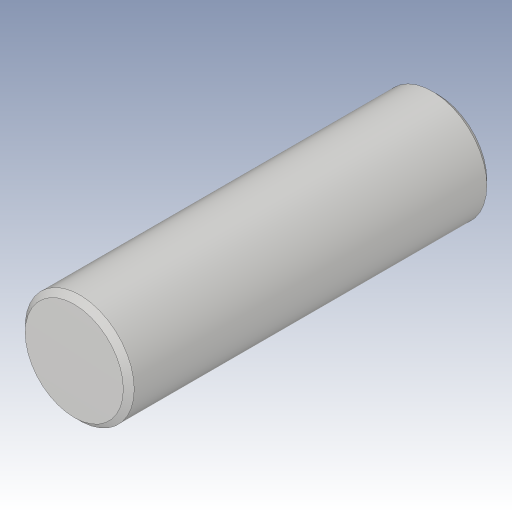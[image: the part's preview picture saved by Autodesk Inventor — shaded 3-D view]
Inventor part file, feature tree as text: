
AUTODESK INVENTOR PART (.ipt)
format: ipt  version: 2023.3 (Build 273359000, 359)  size: 141,312 bytes
history: native  units: in
note: dims shown in document units (in); Inventor stores cm internally (conversion verified against a paired STEP export)
features: extrude x1, chamfer x1, sketch x1
ambient origin geometry x8: Origin, YZ Plane, XZ Plane, XY Plane, X Axis, Y Axis, Z Axis, Center Point
bodies: Body1 (feature_tree)
feature tree (3):
  extrude  "Extrusion3"  Depth=0.7874in TaperAngle=0.0deg
  chamfer  "Fase1"  Distance=0.0118in Angle=45.0deg
  sketch  "Skizze3"  dims[d4=0.2362in d5=0.7874in d6=0.0in d7=0.0118in d8=0.0787in d9=45.0deg]
